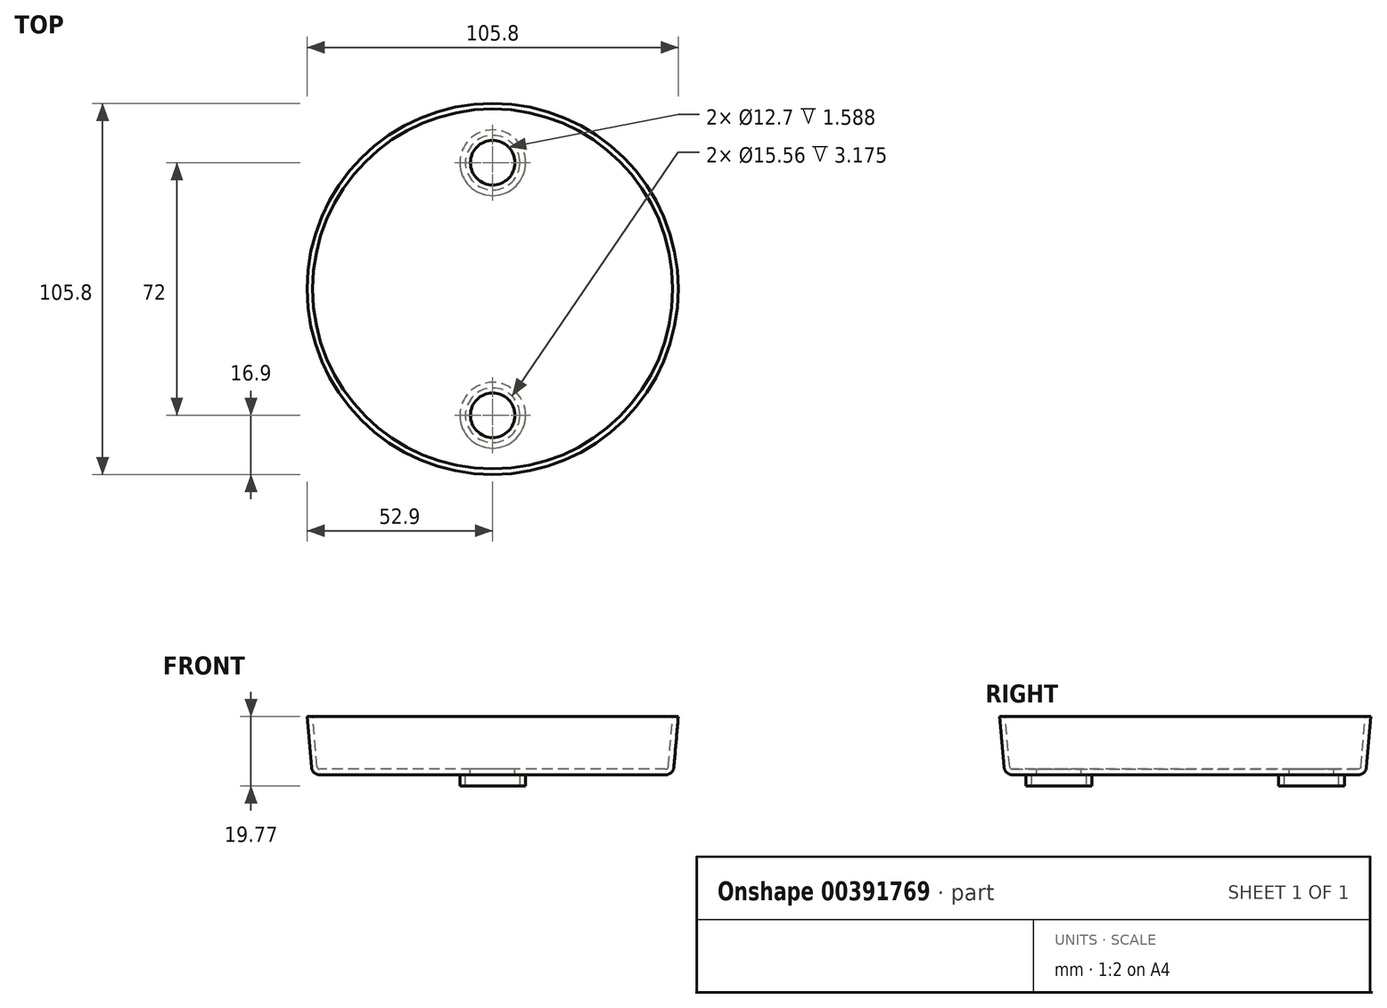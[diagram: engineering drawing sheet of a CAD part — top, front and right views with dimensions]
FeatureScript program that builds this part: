
annotation { "Feature Type Name" : "Feature", "Feature Type Description" : "" }
export const myFeature = defineFeature(function(context is Context, id is Id, definition is map)
    precondition{}
    {
        {
            var Q0;
            Q0=qCreatedBy(makeId("Front.planeOp"),FACE);
            var sketch = newSketch(context, id + "F0", { "sketchPlane" : qUnion([Q0])});
            skLineSegment(sketch, "E0", {"start": v(0, 0) * mm, "end": v(49.27, 0) * mm});
            skLineSegment(sketch, "E1", {"start": v(51.64, 2.17) * mm, "end": v(52.9, 16.59) * mm});
            skLineSegment(sketch, "E2", {"start": v(52.9, 16.59) * mm, "end": v(51.31, 16.59) * mm});
            skLineSegment(sketch, "E3", {"start": v(51.31, 16.59) * mm, "end": v(50.06, 2.31) * mm});
            skLineSegment(sketch, "E4", {"start": v(49.27, 1.59) * mm, "end": v(0, 1.59) * mm});
            skLineSegment(sketch, "E5", {"start": v(0, 1.59) * mm, "end": v(0, 0) * mm});
            skPoint(sketch, "E6.visualSharp", {"position": v(50, 1.59) * mm});
            skArc(sketch, "E6.filletArc", {"start": v(49.27, 1.59) * mm, "mid": v(49.8, 1.8) * mm, "end": v(50.06, 2.31) * mm});
            skPoint(sketch, "E7.visualSharp", {"position": v(51.45, 0) * mm});
            skArc(sketch, "E7.filletArc", {"start": v(49.27, 0) * mm, "mid": v(50.88, 0.63) * mm, "end": v(51.64, 2.17) * mm});
            skSolve(sketch);
        }
        {
            var Q0;
            Q0 = qSketchRegion(id + "F0", true);
            var Q1;
            Q1=sQuery(id+"F0.wireOp",EDGE,"E5");
            revolve(context, id + "F1", {"entities" : qUnion([Q0]), "axis" : qUnion([Q1]), "revolveType" : RevolveType.FULL});
        }
        {
            var Q0;
            Q0=makeQuery(id+"F1.opRevolve","SWEPT_FACE",FACE,{"disambiguationData":[OSD([sQuery(id+"F0.wireOp",EDGE,"E4")])]});
            var sketch = newSketch(context, id + "F2", { "sketchPlane" : qUnion([Q0])});
            skCircle(sketch, "E8", {"center": v(0, 36) * mm, "radius": 6.35 * mm});
            skCircle(sketch, "E9", {"center": v(0, -36) * mm, "radius": 6.35 * mm});
            skSolve(sketch);
        }
        {
            var Q0;
            Q0 = qSketchRegion(id + "F2", true);
            extrude(context, id + "F3", {"entities" : qUnion([Q0]), "operationType" : NewBodyOperationType.REMOVE, "endBound" : BoundingType.THROUGH_ALL, "oppositeDirection" : true, "depth" : 25.4 * mm});
        }
        {
            var Q0;
            Q0=makeQuery(id+"F1.opRevolve","SWEPT_FACE",FACE,{"disambiguationData":[OSD([sQuery(id+"F0.wireOp",EDGE,"E0")])]});
            var sketch = newSketch(context, id + "F4", { "sketchPlane" : qUnion([Q0])});
            skCircle(sketch, "E10", {"center": v(0, -36) * mm, "radius": 7.78 * mm});
            skCircle(sketch, "E11", {"center": v(0, 36) * mm, "radius": 7.78 * mm});
            skCircle(sketch, "E12.0", {"center": v(0, -36) * mm, "radius": 9.37 * mm});
            skCircle(sketch, "E13.0", {"center": v(0, 36) * mm, "radius": 9.37 * mm});
            skSolve(sketch);
        }
        {
            var Q0;
            Q0 = qSketchRegion(id + "F4", true);
            extrude(context, id + "F5", {"entities" : qUnion([Q0]), "operationType" : NewBodyOperationType.ADD, "depth" : 3.17 * mm});
        }
    });
